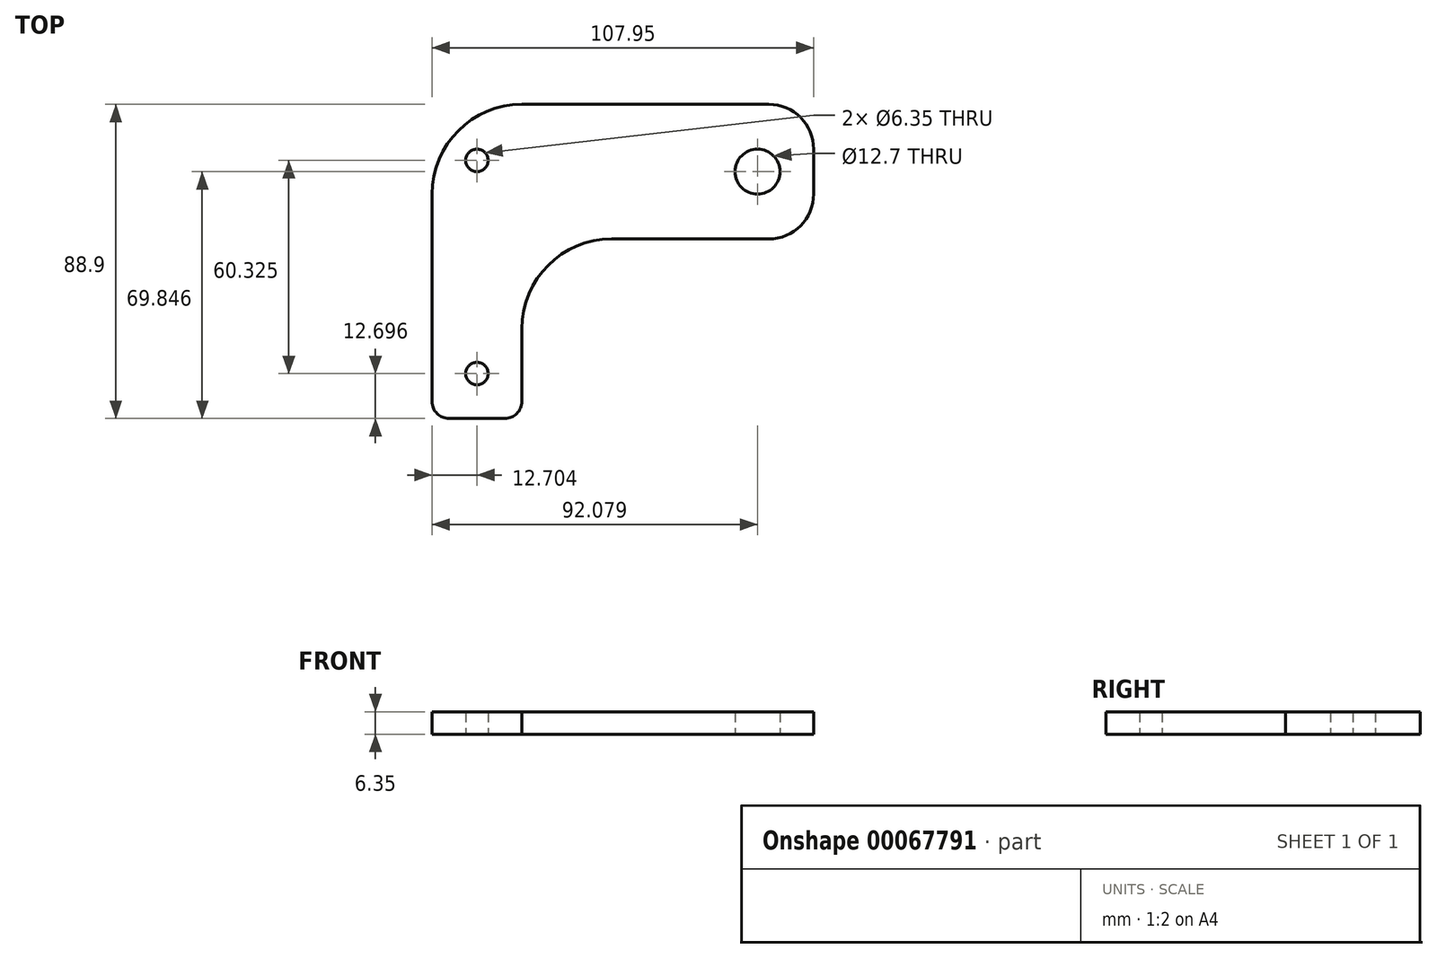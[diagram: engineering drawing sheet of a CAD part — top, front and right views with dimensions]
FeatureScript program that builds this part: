
annotation { "Feature Type Name" : "Feature", "Feature Type Description" : "" }
export const myFeature = defineFeature(function(context is Context, id is Id, definition is map)
    precondition{}
    {
        {
            var Q0;
            Q0=qCreatedBy(makeId("Top.planeOp"),FACE);
            var sketch = newSketch(context, id + "F0", { "sketchPlane" : qUnion([Q0])});
            skLineSegment(sketch, "E0", {"start": v(-52.82, 65.9) * mm, "end": v(55.13, 65.9) * mm});
            skLineSegment(sketch, "E1", {"start": v(55.13, 65.9) * mm, "end": v(55.13, 27.8) * mm});
            skLineSegment(sketch, "E2", {"start": v(55.13, 27.8) * mm, "end": v(-27.42, 27.8) * mm});
            skLineSegment(sketch, "E3", {"start": v(-27.42, 27.8) * mm, "end": v(-27.42, -23) * mm});
            skLineSegment(sketch, "E4", {"start": v(-27.42, -23) * mm, "end": v(-52.82, -23) * mm});
            skLineSegment(sketch, "E5", {"start": v(-52.82, -23) * mm, "end": v(-52.82, 65.9) * mm});
            skSolve(sketch);
        }
        {
            var Q0;
            Q0=makeQuery(id+"F0.imprint","IMPRINT",FACE,{"disambiguationData":[TD([[makeQuery(id+"F0.imprint","IMPRINT",EDGE,{"derivedFrom":sQuery(id+"F0.wireOp",EDGE,"E0")}),-1.0]])]});
            extrude(context, id + "F1", {"entities" : qUnion([Q0]), "depth" : 6.35 * mm});
        }
        {
            var Q0;
            Q0=makeQuery(id+"F1.opExtrude","SWEPT_EDGE",EDGE,{"disambiguationData":[OSD([sQuery(id+"F0.wireOp",EDGE,"E0"),sQuery(id+"F0.wireOp",EDGE,"E5")])]});
            fillet(context, id + "F2", {"entities" : qUnion([Q0]), "radius" : 25.4 * mm, "tangentPropagation" : true, "allowEdgeOverflow" : false});
        }
        {
            var Q0;
            Q0=makeQuery(id+"F1.opExtrude","SWEPT_EDGE",EDGE,{"disambiguationData":[OSD([sQuery(id+"F0.wireOp",EDGE,"E0"),sQuery(id+"F0.wireOp",EDGE,"E1")])]});
            var Q1;
            Q1=makeQuery(id+"F1.opExtrude","SWEPT_EDGE",EDGE,{"disambiguationData":[OSD([sQuery(id+"F0.wireOp",EDGE,"E1"),sQuery(id+"F0.wireOp",EDGE,"E2")])]});
            fillet(context, id + "F3", {"entities" : qUnion([Q0, Q1]), "radius" : 12.7 * mm, "tangentPropagation" : true, "allowEdgeOverflow" : false});
        }
        {
            var Q0;
            Q0=makeQuery(id+"F1.opExtrude","SWEPT_EDGE",EDGE,{"disambiguationData":[OSD([sQuery(id+"F0.wireOp",EDGE,"E2"),sQuery(id+"F0.wireOp",EDGE,"E3")])]});
            fillet(context, id + "F4", {"entities" : qUnion([Q0]), "radius" : 25.4 * mm, "tangentPropagation" : true, "allowEdgeOverflow" : false});
        }
        {
            var Q0;
            Q0=makeQuery(id+"F1.opExtrude","SWEPT_EDGE",EDGE,{"disambiguationData":[OSD([sQuery(id+"F0.wireOp",EDGE,"E3"),sQuery(id+"F0.wireOp",EDGE,"E4")])]});
            var Q1;
            Q1=makeQuery(id+"F1.opExtrude","SWEPT_EDGE",EDGE,{"disambiguationData":[OSD([sQuery(id+"F0.wireOp",EDGE,"E4"),sQuery(id+"F0.wireOp",EDGE,"E5")])]});
            fillet(context, id + "F5", {"entities" : qUnion([Q0, Q1]), "radius" : 4.78 * mm, "tangentPropagation" : true, "allowEdgeOverflow" : false});
        }
        {
            var Q0;
            Q0=qCreatedBy(makeId("Top.planeOp"),FACE);
            var sketch = newSketch(context, id + "F6", { "sketchPlane" : qUnion([Q0])});
            skCircle(sketch, "E6", {"center": v(39.26, 46.85) * mm, "radius": 6.43 * mm});
            skSolve(sketch);
        }
        {
            var Q0;
            Q0=sQuery(id+"F6.wireOp",VERTEX,"E6.center");
            var Q1;
            Q1=makeQuery(id+"F1.opExtrude","SWEPT_BODY",BODY,{"disambiguationData":[OSD([sQuery(id+"F0.wireOp",EDGE,"E0"),sQuery(id+"F0.wireOp",EDGE,"E1"),sQuery(id+"F0.wireOp",EDGE,"E2"),sQuery(id+"F0.wireOp",EDGE,"E3"),sQuery(id+"F0.wireOp",EDGE,"E4"),sQuery(id+"F0.wireOp",EDGE,"E5")])]});
            hole(context, id + "F7", {"style" : HoleStyle.SIMPLE, "holeDiameter" : 12.7 * mm, "endStyle" : HoleEndStyle.THROUGH, "oppositeDirection" : true, "locations" : qUnion([Q0]), "scope" : qUnion([Q1])});
        }
        {
            var Q0;
            Q0=qCreatedBy(makeId("Top.planeOp"),FACE);
            var sketch = newSketch(context, id + "F8", { "sketchPlane" : qUnion([Q0])});
            skCircle(sketch, "E7", {"center": v(-40.12, -10.3) * mm, "radius": 4.16 * mm});
            skSolve(sketch);
        }
        {
            var Q0;
            Q0=sQuery(id+"F8.wireOp",VERTEX,"E7.center");
            var Q1;
            Q1=makeQuery(id+"F1.opExtrude","SWEPT_BODY",BODY,{"disambiguationData":[OSD([sQuery(id+"F0.wireOp",EDGE,"E0"),sQuery(id+"F0.wireOp",EDGE,"E1"),sQuery(id+"F0.wireOp",EDGE,"E2"),sQuery(id+"F0.wireOp",EDGE,"E3"),sQuery(id+"F0.wireOp",EDGE,"E4"),sQuery(id+"F0.wireOp",EDGE,"E5")])]});
            hole(context, id + "F9", {"style" : HoleStyle.SIMPLE, "holeDiameter" : 6.35 * mm, "endStyle" : HoleEndStyle.THROUGH, "oppositeDirection" : true, "locations" : qUnion([Q0]), "scope" : qUnion([Q1])});
        }
        {
            var Q0;
            Q0=qCreatedBy(makeId("Top.planeOp"),FACE);
            var sketch = newSketch(context, id + "F10", { "sketchPlane" : qUnion([Q0])});
            skCircle(sketch, "E8", {"center": v(-40.12, 50.02) * mm, "radius": 4.42 * mm});
            skSolve(sketch);
        }
        {
            var Q0;
            Q0=sQuery(id+"F10.wireOp",VERTEX,"E8.center");
            var Q1;
            Q1=makeQuery(id+"F1.opExtrude","SWEPT_BODY",BODY,{"disambiguationData":[OSD([sQuery(id+"F0.wireOp",EDGE,"E0"),sQuery(id+"F0.wireOp",EDGE,"E1"),sQuery(id+"F0.wireOp",EDGE,"E2"),sQuery(id+"F0.wireOp",EDGE,"E3"),sQuery(id+"F0.wireOp",EDGE,"E4"),sQuery(id+"F0.wireOp",EDGE,"E5")])]});
            hole(context, id + "F11", {"style" : HoleStyle.SIMPLE, "holeDiameter" : 6.35 * mm, "endStyle" : HoleEndStyle.THROUGH, "oppositeDirection" : true, "locations" : qUnion([Q0]), "scope" : qUnion([Q1])});
        }
    });
